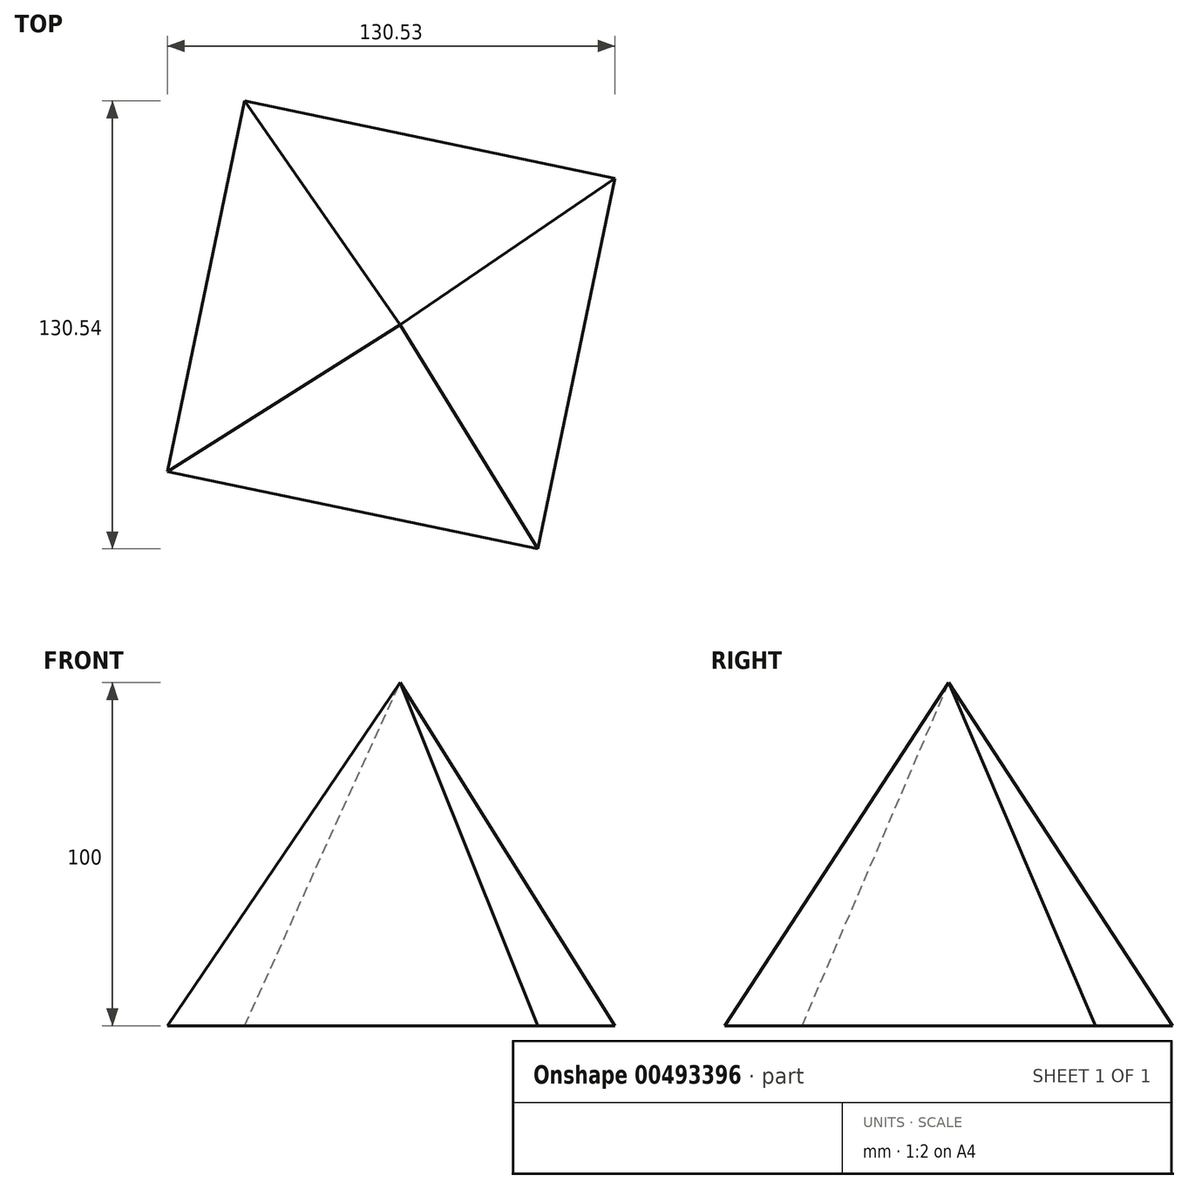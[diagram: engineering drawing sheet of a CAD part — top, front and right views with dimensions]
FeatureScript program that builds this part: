
annotation { "Feature Type Name" : "Feature", "Feature Type Description" : "" }
export const myFeature = defineFeature(function(context is Context, id is Id, definition is map)
    precondition{}
    {
        {
            var Q0;
            Q0=qCreatedBy(makeId("Top.planeOp"),FACE);
            var sketch = newSketch(context, id + "F0", { "sketchPlane" : qUnion([Q0])});
            skCircle(sketch, "E0.cCircle", {"center": v(-2.58, 0) * mm, "radius": 78.02 * mm, "construction": true});
            skLineSegment(sketch, "E0.0", {"start": v(-45.33, 65.27) * mm, "end": v(62.68, 42.75) * mm});
            skLineSegment(sketch, "E0.1", {"start": v(62.68, 42.75) * mm, "end": v(40.16, -65.27) * mm});
            skLineSegment(sketch, "E0.2", {"start": v(40.16, -65.27) * mm, "end": v(-67.85, -42.75) * mm});
            skLineSegment(sketch, "E0.3", {"start": v(-67.85, -42.75) * mm, "end": v(-45.33, 65.27) * mm});
            skSolve(sketch);
        }
        {
            var Q0;
            Q0=qCreatedBy(makeId("Top.planeOp"),FACE);
            cPlane(context, id + "F1", {"entities" : qUnion([Q0]), "cplaneType" : CPlaneType.OFFSET, "offset" : 100 * mm, "width" : 150 * mm, "height" : 150 * mm});
        }
        {
            var Q0;
            Q0=qCreatedBy(id+"F1.planeOp",FACE);
            var sketch = newSketch(context, id + "F2", { "sketchPlane" : qUnion([Q0])});
            skPoint(sketch, "E1", {"position": v(0, 0) * mm});
            skSolve(sketch);
        }
        {
            var Q0;
            Q0=makeQuery(id+"F0.imprint","IMPRINT",FACE,{"disambiguationData":[TD([[makeQuery(id+"F0.imprint","IMPRINT",EDGE,{"derivedFrom":sQuery(id+"F0.wireOp",EDGE,"E0.0")}),-1.0]])]});
            var Q1;
            Q1=sQuery(id+"F2.wireOp",VERTEX,"E1");
            loft(context, id + "F3", {"sheetProfilesArray" : [{ "sheetProfileEntities" : qUnion([Q0]) }, { "sheetProfileEntities" : qUnion([Q1]) }]});
        }
    });
